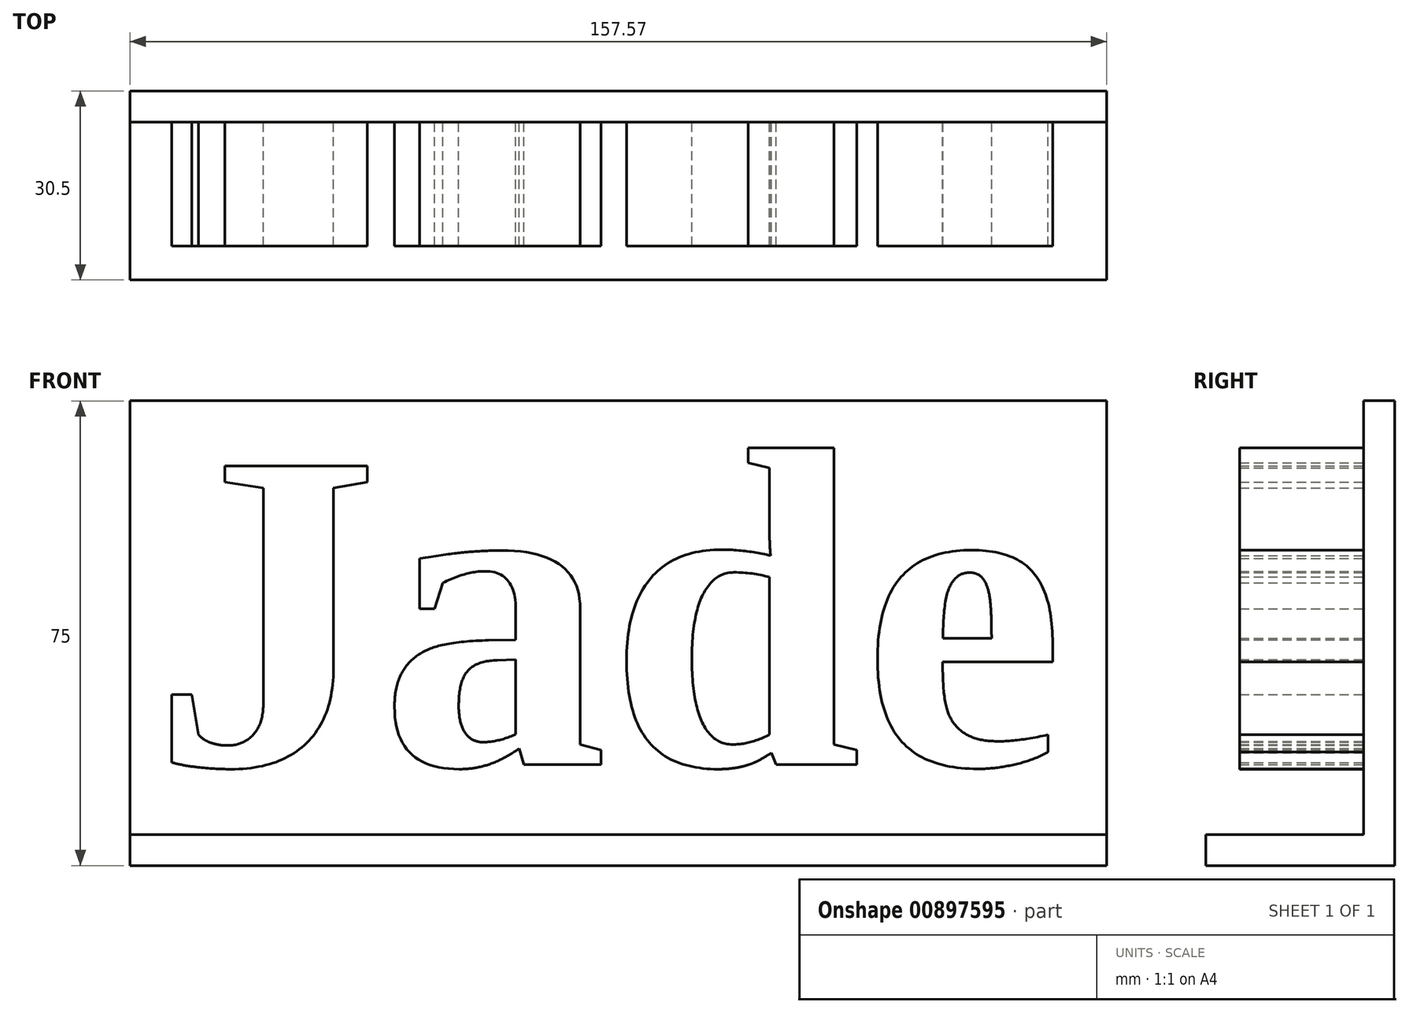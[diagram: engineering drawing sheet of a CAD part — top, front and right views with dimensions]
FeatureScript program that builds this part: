
annotation { "Feature Type Name" : "Feature", "Feature Type Description" : "" }
export const myFeature = defineFeature(function(context is Context, id is Id, definition is map)
    precondition{}
    {
        {
            var Q0;
            Q0=qCreatedBy(makeId("Front.planeOp"),FACE);
            var sketch = newSketch(context, id + "F0", { "sketchPlane" : qUnion([Q0])});
            skText(sketch, "E0", { "text": "Jade", "fontName": "Tinos-Bold.ttf"});
            const initialGuessF0  = {"E0": [-0.05902, -0.01466, 1, 0, 0.05303]};
            skSetInitialGuess(sketch, initialGuessF0);
            skSolve(sketch);
        }
        {
            var Q0;
            Q0 = qSketchRegion(id + "F0", true);
            extrude(context, id + "F1", {"entities" : qUnion([Q0]), "depth" : 25 * mm, "offsetDistance" : 25 * mm});
        }
        {
            var Q0;
            Q0=qCreatedBy(makeId("Front.planeOp"),FACE);
            var sketch = newSketch(context, id + "F2", { "sketchPlane" : qUnion([Q0])});
            skLineSegment(sketch, "E1.bottom", {"start": v(-62.5, 44.06) * mm, "end": v(95.07, 44.06) * mm});
            skLineSegment(sketch, "E1.top", {"start": v(-62.5, -25.94) * mm, "end": v(95.07, -25.94) * mm});
            skLineSegment(sketch, "E1.left", {"start": v(-62.5, 44.06) * mm, "end": v(-62.5, -25.94) * mm});
            skLineSegment(sketch, "E1.right", {"start": v(95.07, 44.06) * mm, "end": v(95.07, -25.94) * mm});
            skSolve(sketch);
        }
        {
            var Q0;
            Q0=makeQuery(id+"F2.imprint","IMPRINT",FACE,{"disambiguationData":[TD([[makeQuery(id+"F2.imprint","IMPRINT",EDGE,{"derivedFrom":sQuery(id+"F2.wireOp",EDGE,"E1.bottom")}),-1.0]])]});
            extrude(context, id + "F3", {"entities" : qUnion([Q0]), "operationType" : NewBodyOperationType.ADD, "depth" : 5 * mm, "offsetDistance" : 25 * mm});
        }
        {
            var Q0;
            Q0=makeQuery(id+"F3.opExtrude","CAP_FACE",FACE,{"disambiguationData":[OSD([sQuery(id+"F2.wireOp",EDGE,"E1.bottom"),sQuery(id+"F2.wireOp",EDGE,"E1.top"),sQuery(id+"F2.wireOp",EDGE,"E1.left"),sQuery(id+"F2.wireOp",EDGE,"E1.right")])],"isStart":true});
            var sketch = newSketch(context, id + "F4", { "sketchPlane" : qUnion([Q0])});
            skLineSegment(sketch, "E2.bottom", {"start": v(-95.07, -25.94) * mm, "end": v(62.5, -25.94) * mm});
            skLineSegment(sketch, "E2.top", {"start": v(-95.07, -30.94) * mm, "end": v(62.5, -30.94) * mm});
            skLineSegment(sketch, "E2.left", {"start": v(-95.07, -25.94) * mm, "end": v(-95.07, -30.94) * mm});
            skLineSegment(sketch, "E2.right", {"start": v(62.5, -25.94) * mm, "end": v(62.5, -30.94) * mm});
            skSolve(sketch);
        }
        {
            var Q0;
            Q0=makeQuery(id+"F4.imprint","IMPRINT",FACE,{"disambiguationData":[TD([[makeQuery(id+"F4.imprint","IMPRINT",EDGE,{"derivedFrom":sQuery(id+"F4.wireOp",EDGE,"E2.bottom")}),1.0]])]});
            extrude(context, id + "F5", {"entities" : qUnion([Q0]), "operationType" : NewBodyOperationType.ADD, "oppositeDirection" : true, "depth" : 30.5 * mm, "offsetDistance" : 25 * mm});
        }
    });
